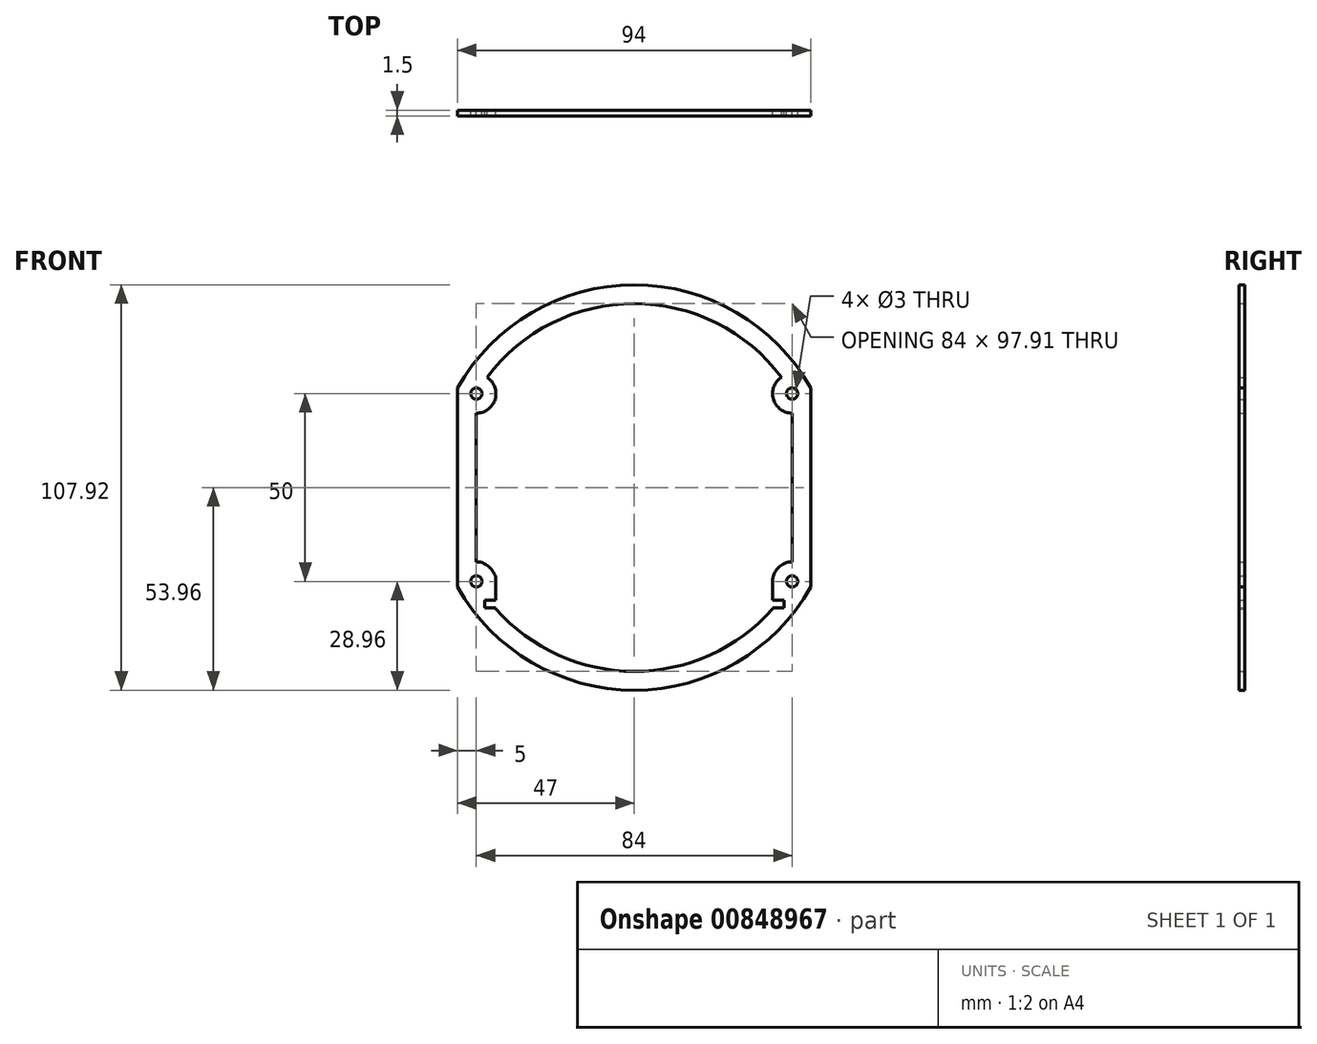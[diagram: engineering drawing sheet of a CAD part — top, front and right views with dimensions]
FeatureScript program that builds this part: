
annotation { "Feature Type Name" : "Feature", "Feature Type Description" : "" }
export const myFeature = defineFeature(function(context is Context, id is Id, definition is map)
    precondition{}
    {
        {
            var Q0;
            Q0=qCreatedBy(makeId("Front.planeOp"),FACE);
            var sketch = newSketch(context, id + "F0", { "sketchPlane" : qUnion([Q0])});
            skPoint(sketch, "E0.middle", {"position": v(0, 0) * mm});
            skCircle(sketch, "E1", {"center": v(-42, 25) * mm, "radius": 1.5 * mm});
            skLineSegment(sketch, "E2.left", {"start": v(-47, 26.5) * mm, "end": v(-47, -26.5) * mm});
            skLineSegment(sketch, "E2.right", {"start": v(47, 26.5) * mm, "end": v(47, -26.5) * mm});
            skArc(sketch, "E3", {"start": v(-39.17, 29.36) * mm, "mid": v(-21.9, 43.78) * mm, "end": v(0, 48.96) * mm});
            skArc(sketch, "E4", {"start": v(-47, 26.5) * mm, "mid": v(-27.22, 46.59) * mm, "end": v(0, 53.96) * mm});
            skArc(sketch, "E5", {"start": v(-39.17, 29.36) * mm, "mid": v(-37.01, 23.53) * mm, "end": v(-42, 19.8) * mm});
            skCircle(sketch, "E6", {"center": v(-42, -25) * mm, "radius": 1.5 * mm});
            skArc(sketch, "E7", {"start": v(-47, -26.5) * mm, "mid": v(-27.22, -46.59) * mm, "end": v(0, -53.96) * mm});
            skLineSegment(sketch, "E8.left", {"start": v(-36.8, -25) * mm, "end": v(-36.8, -30) * mm});
            skLineSegment(sketch, "E9.bottom", {"start": v(-36.8, -30) * mm, "end": v(-39.8, -30) * mm});
            skLineSegment(sketch, "E9.top", {"start": v(-36.8, -32) * mm, "end": v(-39.8, -32) * mm});
            skLineSegment(sketch, "E9.right", {"start": v(-39.8, -30) * mm, "end": v(-39.8, -32) * mm});
            skArc(sketch, "E10", {"start": v(-36.8, -25) * mm, "mid": v(-38.32, -21.32) * mm, "end": v(-42, -19.8) * mm});
            skLineSegment(sketch, "E11", {"start": v(-37.05, -32) * mm, "end": v(-36.8, -32) * mm});
            skLineSegment(sketch, "E12", {"start": v(-36.8, -32.29) * mm, "end": v(-36.8, -32) * mm});
            skArc(sketch, "E13", {"start": v(-36.8, -32.29) * mm, "mid": v(-20.2, -44.6) * mm, "end": v(0, -48.96) * mm});
            skLineSegment(sketch, "E14", {"start": v(-42, 19.8) * mm, "end": v(-42, -19.8) * mm});
            skLineSegment(sketch, "E15", {"start": v(0, 63.92) * mm, "end": v(0, -61.44) * mm, "construction": true});
            skArc(sketch, "E16.MirrorCS", {"start": v(39.17, 29.36) * mm, "mid": v(21.9, 43.78) * mm, "end": v(0, 48.96) * mm});
            skArc(sketch, "E17.MirrorCS", {"start": v(47, 26.5) * mm, "mid": v(27.22, 46.59) * mm, "end": v(0, 53.96) * mm});
            skCircle(sketch, "E18.MirrorC", {"center": v(42, 25) * mm, "radius": 1.5 * mm});
            skArc(sketch, "E19.MirrorCS", {"start": v(39.17, 29.36) * mm, "mid": v(37.01, 23.53) * mm, "end": v(42, 19.8) * mm});
            skArc(sketch, "E20.MirrorCS", {"start": v(36.8, -25) * mm, "mid": v(38.32, -21.32) * mm, "end": v(42, -19.8) * mm});
            skLineSegment(sketch, "E21.MirrorCS", {"start": v(36.8, -25) * mm, "end": v(36.8, -30) * mm});
            skLineSegment(sketch, "E22.MirrorCS", {"start": v(36.8, -30) * mm, "end": v(39.8, -30) * mm});
            skLineSegment(sketch, "E23.MirrorCS", {"start": v(39.8, -30) * mm, "end": v(39.8, -32) * mm});
            skLineSegment(sketch, "E24.MirrorCS", {"start": v(36.8, -32) * mm, "end": v(39.8, -32) * mm});
            skLineSegment(sketch, "E25.MirrorCS", {"start": v(37.05, -32) * mm, "end": v(36.8, -32) * mm});
            skLineSegment(sketch, "E26.MirrorCS", {"start": v(36.8, -32.29) * mm, "end": v(36.8, -32) * mm});
            skLineSegment(sketch, "E27.MirrorCS", {"start": v(42, 19.8) * mm, "end": v(42, -19.8) * mm});
            skArc(sketch, "E28.MirrorCS", {"start": v(36.8, -32.29) * mm, "mid": v(20.2, -44.6) * mm, "end": v(0, -48.96) * mm});
            skArc(sketch, "E29.MirrorCS", {"start": v(47, -26.5) * mm, "mid": v(27.22, -46.59) * mm, "end": v(0, -53.96) * mm});
            skCircle(sketch, "E30.MirrorC", {"center": v(42, -25) * mm, "radius": 1.5 * mm});
            skSolve(sketch);
        }
        {
            var Q0;
            Q0=makeQuery(id+"F0.imprint","IMPRINT",FACE,{"disambiguationData":[TD([[makeQuery(id+"F0.imprint","IMPRINT",EDGE,{"derivedFrom":sQuery(id+"F0.wireOp",EDGE,"E1")}),-1.0]])]});
            extrude(context, id + "F1", {"entities" : qUnion([Q0]), "depth" : 1.5 * mm, "offsetDistance" : 25 * mm});
        }
    });
